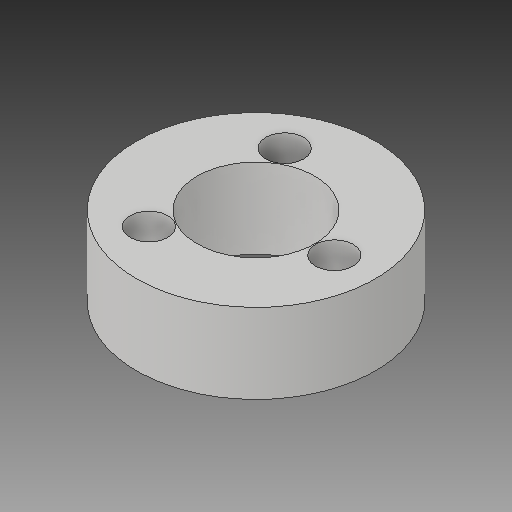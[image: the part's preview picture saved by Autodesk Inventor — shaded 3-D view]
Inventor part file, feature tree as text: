
AUTODESK INVENTOR PART (.ipt)
format: ipt  version: 2018 (Build 220112000, 112)  size: 106,496 bytes
history: native  units: in
note: dims shown in document units (in); Inventor stores cm internally (conversion verified against a paired STEP export)
features: extrude x2, sketch x2
ambient origin geometry x8: Origin, YZ Plane, XZ Plane, XY Plane, X Axis, Y Axis, Z Axis, Center Point
bodies: Solid1 (feature_tree)
feature tree (4):
  extrude  "Extrusion1"  Depth=1.5795in TaperAngle=360.0deg
  extrude  "Extrusion2"  [1 undecoded]
  sketch  "Sketch1"  dims[d5=1.5795in d6=0.0in d11=1.1811in d13=360.0deg]
  sketch  "Sketch2"  dims[d16=1.5795in d17=0.0in]
note: 1 required parameter value undecoded (feature->parameter linkage not recoverable at this tier; creation-order binding heuristic only, values carry confidence <= 0.55)
